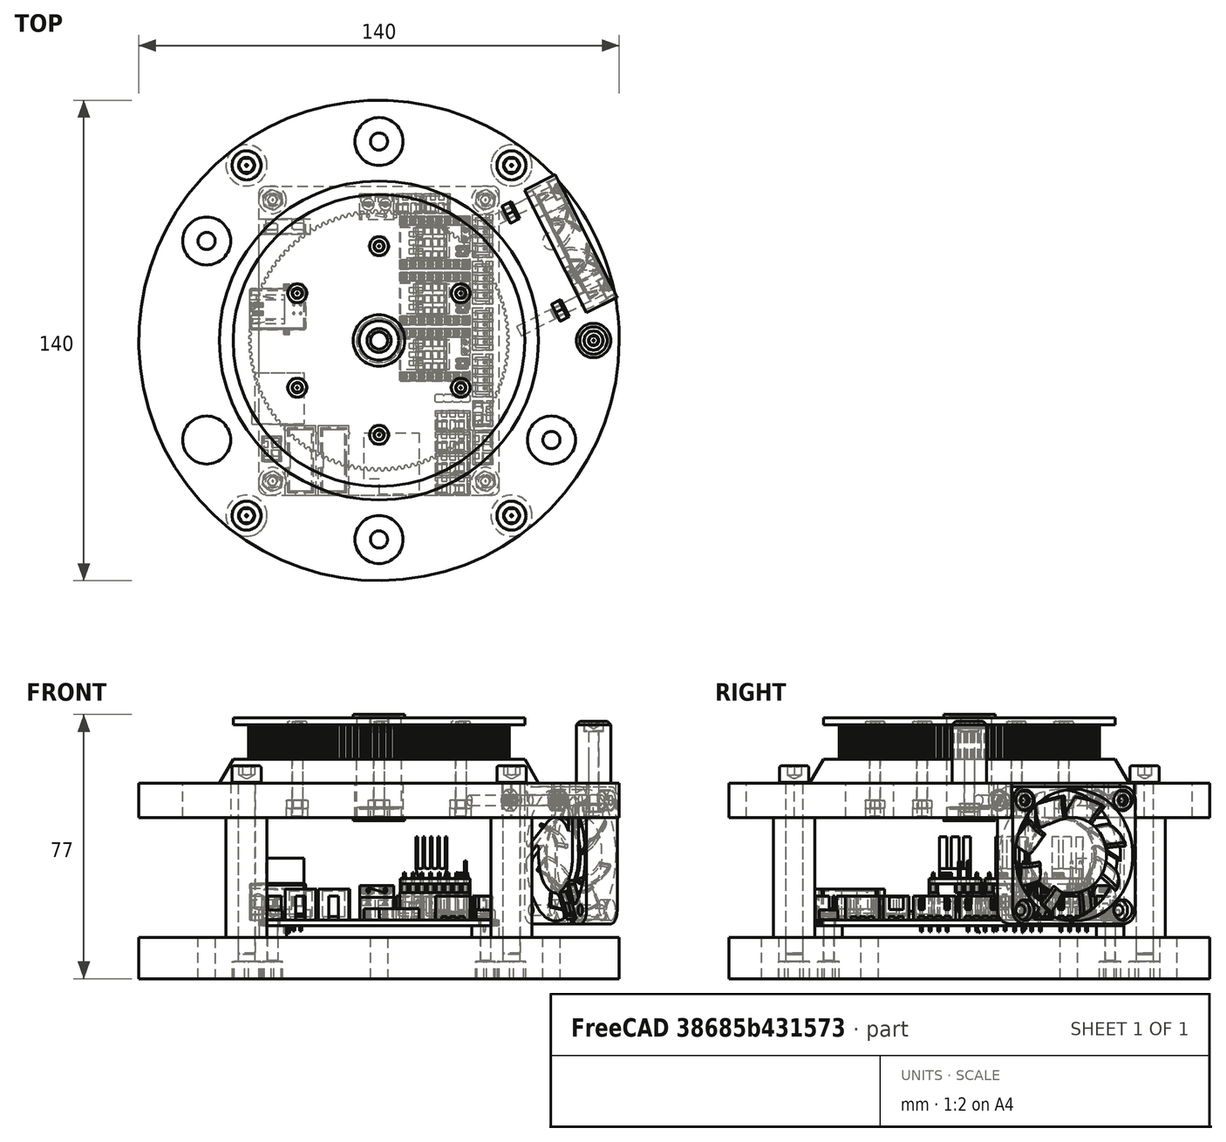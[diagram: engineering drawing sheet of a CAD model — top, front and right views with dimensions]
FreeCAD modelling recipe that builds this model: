
FCSTD DOCUMENT  (FreeCAD 0.20R29410 (Git))
Label: #0_ASSEMBLY_MAIN_BASE
License: All rights reserved
LicenseURL: http://en.wikipedia.org/wiki/All_rights_reserved
objects: Part::FeaturePython×38, App::FeaturePython×33
note: 38 computed .brp shape members not serialized (recipe doc carries the construction recipe); baked Part::Feature solids carry a one-line shape summary decoded from their .brp

FEATURE [Part::FeaturePython] b__1_BaseFloor_001_  label="#1_BaseFloor_001"  # a2plus imported part (geometry in sourceFile) (typed FeaturePython)
  a2p_Version = 0.4.60k
  fixedPosition = true
  objectType = a2pPart
  sourceFile = .\#1_BaseFloor.FCStd
  subassemblyImport = false
  timeLastImport = 1.68285e+09
  updateColors = true
FEATURE [Part::FeaturePython] b__2_BaseSpacers_001_  label="#2_BaseSpacers_001"  # a2plus imported part (geometry in sourceFile) (typed FeaturePython)
  Placement = pos=(38.6,-51.05,12) rot=(0,0,1;0rad)
  a2p_Version = 0.4.60k
  fixedPosition = false
  objectType = a2pPart
  sourceFile = .\#2_BaseSpacers.FCStd
  subassemblyImport = false
  timeLastImport = 1.68285e+09
  updateColors = true
FEATURE [Part::FeaturePython] b__3_BaseTop_001_  label="#3_BaseTop_001"  # a2plus imported part (geometry in sourceFile) (typed FeaturePython)
  Placement = pos=(-9e-15,-7.13554e-09,47) rot=(0,0,1;0rad)
  a2p_Version = 0.4.60k
  fixedPosition = false
  objectType = a2pPart
  sourceFile = .\#3_BaseTop.FCStd
  subassemblyImport = false
  timeLastImport = 1.68294e+09
  updateColors = true
FEATURE [Part::FeaturePython] b__2_BaseSpacers_001_001  label="#2_BaseSpacers_002"  # a2plus imported part (geometry in sourceFile) (typed FeaturePython)
  Placement = pos=(-38.6,-51.05,12) rot=(0,0,1;0rad)
  a2p_Version = 0.4.60k
  fixedPosition = false
  objectType = a2pPart
  sourceFile = .\#2_BaseSpacers.FCStd
  subassemblyImport = false
  timeLastImport = 1.68285e+09
  updateColors = true
FEATURE [Part::FeaturePython] b__2_BaseSpacers_001_002  label="#2_BaseSpacers_003"  # a2plus imported part (geometry in sourceFile) (typed FeaturePython)
  Placement = pos=(-38.6,51.05,12) rot=(0,0,1;0rad)
  a2p_Version = 0.4.60k
  fixedPosition = false
  objectType = a2pPart
  sourceFile = .\#2_BaseSpacers.FCStd
  subassemblyImport = false
  timeLastImport = 1.68285e+09
  updateColors = true
FEATURE [Part::FeaturePython] b__2_BaseSpacers_001_003  label="#2_BaseSpacers_004"  # a2plus imported part (geometry in sourceFile) (typed FeaturePython)
  Placement = pos=(38.6,51.05,12) rot=(0,0,1;0rad)
  a2p_Version = 0.4.60k
  fixedPosition = false
  objectType = a2pPart
  sourceFile = .\#2_BaseSpacers.FCStd
  subassemblyImport = false
  timeLastImport = 1.68285e+09
  updateColors = true
FEATURE [Part::FeaturePython] b_404010_Fan_v51_001_  label="4010Fan"  # a2plus imported part (geometry in sourceFile) (typed FeaturePython)
  Placement = pos=(51.4397,25.9841,36) rot=(0,0,-1;1.10305rad)
  a2p_Version = 0.4.60k
  fixedPosition = false
  objectType = a2pPart
  sourceFile = .\..\..\..\..\..\Downloads\404010 Fan v5.step
  subassemblyImport = false
  timeLastImport = 1.68849e+09
  updateColors = true
FEATURE [App::FeaturePython] circularEdge_001  label="circularEdge_001__#3_BaseTop_001"  # a2plus constraint (typed FeaturePython)
  Object1 = b_404010_Fan_v51_001_
  Object2 = b__3_BaseTop_001_
  ParentTreeObject = -> b_404010_Fan_v51_001_
  SubElement1 = Edge119
  SubElement2 = Edge96
  Suppressed = false
  Type = circularEdge
  directionConstraint = 1
  lockRotation = false
  offset = 0
FEATURE [App::FeaturePython] circularEdge_001_mirror  label="circularEdge_001__404010 Fan v51_001"  # a2plus constraint (typed FeaturePython)
  Object1 = b_404010_Fan_v51_001_
  Object2 = b__3_BaseTop_001_
  ParentTreeObject = -> b__3_BaseTop_001_
  SubElement1 = Edge119
  SubElement2 = Edge96
  Suppressed = false
  Type = circularEdge
  directionConstraint = 1
  lockRotation = false
  offset = 0
FEATURE [Part::FeaturePython] b__4_BasePulley120T_001_  label="#4_BasePulley120T_001"  # a2plus imported part (geometry in sourceFile) (typed FeaturePython)
  Placement = pos=(-38.1972,-38.1972,64) rot=(0,0,1;0rad)
  a2p_Version = 0.4.60k
  fixedPosition = false
  objectType = a2pPart
  sourceFile = .\#4_BasePulley120T.FCStd
  subassemblyImport = false
  timeLastImport = 1.68293e+09
  updateColors = true
FEATURE [App::FeaturePython] circularEdge_002  label="circularEdge_002__#3_BaseTop_001"  # a2plus constraint (typed FeaturePython)
  Object1 = b__4_BasePulley120T_001_
  Object2 = b__3_BaseTop_001_
  ParentTreeObject = -> b__4_BasePulley120T_001_
  SubElement1 = Edge2542
  SubElement2 = Edge151
  Suppressed = false
  Type = circularEdge
  directionConstraint = 0
  lockRotation = false
  offset = 0
FEATURE [App::FeaturePython] circularEdge_002_mirror  label="circularEdge_002__#4_BasePulley120T_001"  # a2plus constraint (typed FeaturePython)
  Object1 = b__4_BasePulley120T_001_
  Object2 = b__3_BaseTop_001_
  ParentTreeObject = -> b__3_BaseTop_001_
  SubElement1 = Edge2542
  SubElement2 = Edge151
  Suppressed = false
  Type = circularEdge
  directionConstraint = 0
  lockRotation = false
  offset = 0
FEATURE [App::FeaturePython] circularEdge_003  label="circularEdge_003__#3_BaseTop_001"  # a2plus constraint (typed FeaturePython)
  Object1 = b__4_BasePulley120T_001_
  Object2 = b__3_BaseTop_001_
  ParentTreeObject = -> b__4_BasePulley120T_001_
  SubElement1 = Edge2542
  SubElement2 = Edge151
  Suppressed = false
  Type = circularEdge
  directionConstraint = 0
  lockRotation = false
  offset = 0
FEATURE [App::FeaturePython] circularEdge_003_mirror  label="circularEdge_003__#4_BasePulley120T_001"  # a2plus constraint (typed FeaturePython)
  Object1 = b__4_BasePulley120T_001_
  Object2 = b__3_BaseTop_001_
  ParentTreeObject = -> b__3_BaseTop_001_
  SubElement1 = Edge2542
  SubElement2 = Edge151
  Suppressed = false
  Type = circularEdge
  directionConstraint = 0
  lockRotation = false
  offset = 0
FEATURE [App::FeaturePython] circularEdge_004  label="circularEdge_004__#1_BaseFloor_001"  # a2plus constraint (typed FeaturePython)
  Object1 = b__2_BaseSpacers_001_
  Object2 = b__1_BaseFloor_001_
  ParentTreeObject = -> b__2_BaseSpacers_001_
  SubElement1 = Edge2
  SubElement2 = Edge60
  Suppressed = false
  Type = circularEdge
  directionConstraint = 0
  lockRotation = false
  offset = 0
FEATURE [App::FeaturePython] circularEdge_004_mirror  label="circularEdge_004__#2_BaseSpacers_001"  # a2plus constraint (typed FeaturePython)
  Object1 = b__2_BaseSpacers_001_
  Object2 = b__1_BaseFloor_001_
  ParentTreeObject = -> b__1_BaseFloor_001_
  SubElement1 = Edge2
  SubElement2 = Edge60
  Suppressed = false
  Type = circularEdge
  directionConstraint = 0
  lockRotation = false
  offset = 0
FEATURE [App::FeaturePython] circularEdge_005  label="circularEdge_005__#2_BaseSpacers_001"  # a2plus constraint (typed FeaturePython)
  Object1 = b__3_BaseTop_001_
  Object2 = b__2_BaseSpacers_001_
  ParentTreeObject = -> b__3_BaseTop_001_
  SubElement1 = Edge24
  SubElement2 = Edge6
  Suppressed = false
  Type = circularEdge
  directionConstraint = 0
  lockRotation = false
  offset = 0
FEATURE [App::FeaturePython] circularEdge_005_mirror  label="circularEdge_005__#3_BaseTop_001"  # a2plus constraint (typed FeaturePython)
  Object1 = b__3_BaseTop_001_
  Object2 = b__2_BaseSpacers_001_
  ParentTreeObject = -> b__2_BaseSpacers_001_
  SubElement1 = Edge24
  SubElement2 = Edge6
  Suppressed = false
  Type = circularEdge
  directionConstraint = 0
  lockRotation = false
  offset = 0
FEATURE [App::FeaturePython] axisCoincident_001  label="axisCoincident_001__#1_BaseFloor_001"  # a2plus constraint (typed FeaturePython)
  Object1 = b__2_BaseSpacers_001_003
  Object2 = b__1_BaseFloor_001_
  ParentTreeObject = -> b__2_BaseSpacers_001_003
  SubElement1 = Edge2
  SubElement2 = Edge69
  Suppressed = false
  Type = axial
  directionConstraint = 0
  lockRotation = false
FEATURE [App::FeaturePython] axisCoincident_001_mirror  label="axisCoincident_001__#2_BaseSpacers_004"  # a2plus constraint (typed FeaturePython)
  Object1 = b__2_BaseSpacers_001_003
  Object2 = b__1_BaseFloor_001_
  ParentTreeObject = -> b__1_BaseFloor_001_
  SubElement1 = Edge2
  SubElement2 = Edge69
  Suppressed = false
  Type = axial
  directionConstraint = 0
  lockRotation = false
FEATURE [App::FeaturePython] circularEdge_006  label="circularEdge_006__#1_BaseFloor_001"  # a2plus constraint (typed FeaturePython)
  Object1 = b__2_BaseSpacers_001_003
  Object2 = b__1_BaseFloor_001_
  ParentTreeObject = -> b__2_BaseSpacers_001_003
  SubElement1 = Edge2
  SubElement2 = Edge69
  Suppressed = false
  Type = circularEdge
  directionConstraint = 0
  lockRotation = false
  offset = 0
FEATURE [App::FeaturePython] circularEdge_006_mirror  label="circularEdge_006__#2_BaseSpacers_004"  # a2plus constraint (typed FeaturePython)
  Object1 = b__2_BaseSpacers_001_003
  Object2 = b__1_BaseFloor_001_
  ParentTreeObject = -> b__1_BaseFloor_001_
  SubElement1 = Edge2
  SubElement2 = Edge69
  Suppressed = false
  Type = circularEdge
  directionConstraint = 0
  lockRotation = false
  offset = 0
FEATURE [App::FeaturePython] circularEdge_007  label="circularEdge_007__#1_BaseFloor_001"  # a2plus constraint (typed FeaturePython)
  Object1 = b__2_BaseSpacers_001_002
  Object2 = b__1_BaseFloor_001_
  ParentTreeObject = -> b__2_BaseSpacers_001_002
  SubElement1 = Edge2
  SubElement2 = Edge65
  Suppressed = false
  Type = circularEdge
  directionConstraint = 0
  lockRotation = false
  offset = 0
FEATURE [App::FeaturePython] circularEdge_007_mirror  label="circularEdge_007__#2_BaseSpacers_003"  # a2plus constraint (typed FeaturePython)
  Object1 = b__2_BaseSpacers_001_002
  Object2 = b__1_BaseFloor_001_
  ParentTreeObject = -> b__1_BaseFloor_001_
  SubElement1 = Edge2
  SubElement2 = Edge65
  Suppressed = false
  Type = circularEdge
  directionConstraint = 0
  lockRotation = false
  offset = 0
FEATURE [App::FeaturePython] circularEdge_008  label="circularEdge_008__#1_BaseFloor_001"  # a2plus constraint (typed FeaturePython)
  Object1 = b__2_BaseSpacers_001_001
  Object2 = b__1_BaseFloor_001_
  ParentTreeObject = -> b__2_BaseSpacers_001_001
  SubElement1 = Edge2
  SubElement2 = Edge57
  Suppressed = false
  Type = circularEdge
  directionConstraint = 0
  lockRotation = false
  offset = 0
FEATURE [App::FeaturePython] circularEdge_008_mirror  label="circularEdge_008__#2_BaseSpacers_002"  # a2plus constraint (typed FeaturePython)
  Object1 = b__2_BaseSpacers_001_001
  Object2 = b__1_BaseFloor_001_
  ParentTreeObject = -> b__1_BaseFloor_001_
  SubElement1 = Edge2
  SubElement2 = Edge57
  Suppressed = false
  Type = circularEdge
  directionConstraint = 0
  lockRotation = false
  offset = 0
FEATURE [Part::FeaturePython] Screw  label="M3x25-Tornillo"  # Fasteners workbench fastener (typed FeaturePython)
  Placement = pos=(-23.8157,-13.75,72) rot=(0,0,1;0rad)
  baseObject = -> b__4_BasePulley120T_001_ [Edge2555]
  diameter = 4
  invert = false
  leftHanded = false
  length = 10
  lengthCustom = 25
  matchOuter = false
  offset = 0
  thread = false
  type = 45
FEATURE [Part::FeaturePython] Screw001  label="M3x25-Tornillo018"  # Fasteners workbench fastener (typed FeaturePython)
  Placement = pos=(-23.8157,13.75,72) rot=(0,0,1;0rad)
  baseObject = -> b__4_BasePulley120T_001_ [Edge2556]
  diameter = 4
  invert = false
  leftHanded = false
  length = 10
  lengthCustom = 25
  matchOuter = false
  offset = 0
  thread = false
  type = 45
FEATURE [Part::FeaturePython] Screw002  label="M3x25-Tornillo019"  # Fasteners workbench fastener (typed FeaturePython)
  Placement = pos=(7.1e-15,27.5,72) rot=(0,0,1;0rad)
  baseObject = -> b__4_BasePulley120T_001_ [Edge2553]
  diameter = 4
  invert = false
  leftHanded = false
  length = 10
  lengthCustom = 25
  matchOuter = false
  offset = 0
  thread = false
  type = 45
FEATURE [Part::FeaturePython] Screw003  label="M3x25-Tornillo020"  # Fasteners workbench fastener (typed FeaturePython)
  Placement = pos=(23.8157,13.75,72) rot=(0,0,1;0rad)
  baseObject = -> b__4_BasePulley120T_001_ [Edge2552]
  diameter = 4
  invert = false
  leftHanded = false
  length = 10
  lengthCustom = 25
  matchOuter = false
  offset = 0
  thread = false
  type = 45
FEATURE [Part::FeaturePython] Screw004  label="M3x25-Tornillo021"  # Fasteners workbench fastener (typed FeaturePython)
  Placement = pos=(23.8157,-13.75,72) rot=(0,0,1;0rad)
  baseObject = -> b__4_BasePulley120T_001_ [Edge2551]
  diameter = 4
  invert = false
  leftHanded = false
  length = 10
  lengthCustom = 25
  matchOuter = false
  offset = 0
  thread = false
  type = 45
FEATURE [Part::FeaturePython] Screw005  label="M3x25-Tornillo022"  # Fasteners workbench fastener (typed FeaturePython)
  Placement = pos=(-7.1e-15,-27.5,72) rot=(0,0,1;0rad)
  baseObject = -> b__4_BasePulley120T_001_ [Edge2554]
  diameter = 4
  invert = false
  leftHanded = false
  length = 10
  lengthCustom = 25
  matchOuter = false
  offset = 0
  thread = false
  type = 45
FEATURE [Part::FeaturePython] Screw006  label="M5x50-Tornillo"  # Fasteners workbench fastener (typed FeaturePython)
  Placement = pos=(38.6,51.05,57) rot=(0,0,1;0rad)
  baseObject = -> b__3_BaseTop_001_ [Edge92]
  diameter = 6
  invert = false
  leftHanded = false
  length = 12
  lengthCustom = 50
  matchOuter = false
  offset = 0
  thread = false
  type = 45
FEATURE [Part::FeaturePython] Screw007  label="M5x50-Tornillo007"  # Fasteners workbench fastener (typed FeaturePython)
  Placement = pos=(38.6,-51.05,57) rot=(0,0,1;0rad)
  baseObject = -> b__3_BaseTop_001_ [Edge77]
  diameter = 6
  invert = false
  leftHanded = false
  length = 12
  lengthCustom = 50
  matchOuter = false
  offset = 0
  thread = false
  type = 45
FEATURE [Part::FeaturePython] Screw008  label="M5x50-Tornillo008"  # Fasteners workbench fastener (typed FeaturePython)
  Placement = pos=(-38.6,-51.05,57) rot=(0,0,1;0rad)
  baseObject = -> b__3_BaseTop_001_ [Edge74]
  diameter = 6
  invert = false
  leftHanded = false
  length = 12
  lengthCustom = 50
  matchOuter = false
  offset = 0
  thread = false
  type = 45
FEATURE [Part::FeaturePython] Screw009  label="M5x50-Tornillo009"  # Fasteners workbench fastener (typed FeaturePython)
  Placement = pos=(-38.6,51.05,57) rot=(0,0,1;0rad)
  baseObject = -> b__3_BaseTop_001_ [Edge81]
  diameter = 6
  invert = false
  leftHanded = false
  length = 12
  lengthCustom = 50
  matchOuter = false
  offset = 0
  thread = false
  type = 45
FEATURE [Part::FeaturePython] Screw010  label="M3x16-Tornillo"  # Fasteners workbench fastener (typed FeaturePython)
  Placement = pos=(64.9019,14.8588,52) rot=(-0.450878,0.892586,0;1.5708rad)
  baseObject = -> b_404010_Fan_v51_001_ [Edge73]
  diameter = 4
  invert = false
  leftHanded = false
  length = 10
  lengthCustom = 16
  matchOuter = false
  offset = 0
  thread = false
  type = 45
FEATURE [Part::FeaturePython] Screw011  label="M3x16-Tornillo001"  # Fasteners workbench fastener (typed FeaturePython)
  Placement = pos=(50.4738,43.4216,52) rot=(-0.450878,0.892586,0;1.5708rad)
  baseObject = -> b_404010_Fan_v51_001_ [Edge61]
  diameter = 4
  invert = false
  leftHanded = false
  length = 10
  lengthCustom = 16
  matchOuter = false
  offset = 0
  thread = false
  type = 45
FEATURE [Part::FeaturePython] b__6_BaseRotationLimit_001_  label="#6_BaseRotationLimit_001"  # a2plus imported part (geometry in sourceFile) (typed FeaturePython)
  Placement = pos=(62.5,-7.13554e-09,57.0012) rot=(0,0,1;0rad)
  a2p_Version = 0.4.60k
  fixedPosition = false
  objectType = a2pPart
  sourceFile = .\#6_BaseRotationLimit.FCStd
  subassemblyImport = false
  timeLastImport = 1.68294e+09
  updateColors = true
FEATURE [App::FeaturePython] circularEdge_009  label="circularEdge_009__#3_BaseTop_001"  # a2plus constraint (typed FeaturePython)
  Object1 = b__6_BaseRotationLimit_001_
  Object2 = b__3_BaseTop_001_
  ParentTreeObject = -> b__6_BaseRotationLimit_001_
  SubElement1 = Edge3
  SubElement2 = Edge83
  Suppressed = false
  Type = circularEdge
  directionConstraint = 0
  lockRotation = false
  offset = 0
FEATURE [App::FeaturePython] circularEdge_009_mirror  label="circularEdge_009__#6_BaseRotationLimit_001"  # a2plus constraint (typed FeaturePython)
  Object1 = b__6_BaseRotationLimit_001_
  Object2 = b__3_BaseTop_001_
  ParentTreeObject = -> b__3_BaseTop_001_
  SubElement1 = Edge3
  SubElement2 = Edge83
  Suppressed = false
  Type = circularEdge
  directionConstraint = 0
  lockRotation = false
  offset = 0
FEATURE [Part::FeaturePython] Screw012  label="M3x25-Tornillo023"  # Fasteners workbench fastener (typed FeaturePython)
  Placement = pos=(62.5,-7.13554e-09,72.0012) rot=(0,0,1;0rad)
  baseObject = -> b__6_BaseRotationLimit_001_ [Edge9]
  diameter = 4
  invert = true
  leftHanded = false
  length = 8
  lengthCustom = 25
  matchOuter = false
  offset = 0
  thread = false
  type = 45
FEATURE [Part::FeaturePython] b_Mks1_001_  label="Mks1_001"  # a2plus imported part (geometry in sourceFile) (typed FeaturePython)
  Placement = pos=(-28.4749,-43.7494,28.3991) rot=(0.57735,0.57735,0.57735;2.0944rad)
  a2p_Version = 0.4.60k
  fixedPosition = false
  objectType = a2pPart
  sourceFile = .\..\..\..\..\..\Downloads\Mks.STEP
  subassemblyImport = false
  timeLastImport = 1.68849e+09
  updateColors = true
FEATURE [App::FeaturePython] circularEdge_010  label="circularEdge_010__#1_BaseFloor_001"  # a2plus constraint (typed FeaturePython)
  Object1 = b_Mks1_001_
  Object2 = b__1_BaseFloor_001_
  ParentTreeObject = -> b_Mks1_001_
  SubElement1 = Edge10771
  SubElement2 = Edge193
  Suppressed = false
  Type = circularEdge
  directionConstraint = 0
  lockRotation = false
  offset = 0
FEATURE [App::FeaturePython] circularEdge_010_mirror  label="circularEdge_010__Mks1_001"  # a2plus constraint (typed FeaturePython)
  Object1 = b_Mks1_001_
  Object2 = b__1_BaseFloor_001_
  ParentTreeObject = -> b__1_BaseFloor_001_
  SubElement1 = Edge10771
  SubElement2 = Edge193
  Suppressed = false
  Type = circularEdge
  directionConstraint = 0
  lockRotation = false
  offset = 0
FEATURE [App::FeaturePython] circularEdge_011  label="circularEdge_011__#1_BaseFloor_001"  # a2plus constraint (typed FeaturePython)
  Object1 = b_Mks1_001_
  Object2 = b__1_BaseFloor_001_
  ParentTreeObject = -> b_Mks1_001_
  SubElement1 = Edge10775
  SubElement2 = Edge194
  Suppressed = false
  Type = circularEdge
  directionConstraint = 0
  lockRotation = false
  offset = 0
FEATURE [App::FeaturePython] circularEdge_011_mirror  label="circularEdge_011__Mks1_001"  # a2plus constraint (typed FeaturePython)
  Object1 = b_Mks1_001_
  Object2 = b__1_BaseFloor_001_
  ParentTreeObject = -> b__1_BaseFloor_001_
  SubElement1 = Edge10775
  SubElement2 = Edge194
  Suppressed = false
  Type = circularEdge
  directionConstraint = 0
  lockRotation = false
  offset = 0
FEATURE [Part::FeaturePython] b_F6951_001_  label="F6951_001"  # a2plus imported part (geometry in sourceFile) (typed FeaturePython)
  Placement = pos=(9.797e-12,-7.14046e-09,73) rot=(0,0,1;0rad)
  a2p_Version = 0.4.60k
  fixedPosition = false
  objectType = a2pPart
  sourceFile = .\..\Complements\F695.step
  subassemblyImport = false
  timeLastImport = 1.6885e+09
  updateColors = true
FEATURE [Part::FeaturePython] b_F6951_001_001  label="F6951_002"  # a2plus imported part (geometry in sourceFile) (typed FeaturePython)
  Placement = pos=(-1.73663e-08,-3.91819e-08,50) rot=(0.879228,-0.476402,0;3.14159rad)
  a2p_Version = 0.4.60k
  fixedPosition = false
  objectType = a2pPart
  sourceFile = .\..\Complements\F695.step
  subassemblyImport = false
  timeLastImport = 1.6885e+09
  updateColors = true
FEATURE [App::FeaturePython] circularEdge_012  label="circularEdge_012__#4_BasePulley120T_001"  # a2plus constraint (typed FeaturePython)
  Object1 = b_F6951_001_
  Object2 = b__4_BasePulley120T_001_
  ParentTreeObject = -> b_F6951_001_
  SubElement1 = Edge18
  SubElement2 = Edge849
  Suppressed = false
  Type = circularEdge
  directionConstraint = 0
  lockRotation = false
  offset = 0
FEATURE [App::FeaturePython] circularEdge_012_mirror  label="circularEdge_012__F6951_001"  # a2plus constraint (typed FeaturePython)
  Object1 = b_F6951_001_
  Object2 = b__4_BasePulley120T_001_
  ParentTreeObject = -> b__4_BasePulley120T_001_
  SubElement1 = Edge18
  SubElement2 = Edge849
  Suppressed = false
  Type = circularEdge
  directionConstraint = 0
  lockRotation = false
  offset = 0
FEATURE [App::FeaturePython] circularEdge_013  label="circularEdge_013__#3_BaseTop_001"  # a2plus constraint (typed FeaturePython)
  Object1 = b_F6951_001_001
  Object2 = b__3_BaseTop_001_
  ParentTreeObject = -> b_F6951_001_001
  SubElement1 = Edge18
  SubElement2 = Edge39
  Suppressed = false
  Type = circularEdge
  directionConstraint = 1
  lockRotation = false
  offset = 0
FEATURE [App::FeaturePython] circularEdge_013_mirror  label="circularEdge_013__F6951_002"  # a2plus constraint (typed FeaturePython)
  Object1 = b_F6951_001_001
  Object2 = b__3_BaseTop_001_
  ParentTreeObject = -> b__3_BaseTop_001_
  SubElement1 = Edge18
  SubElement2 = Edge39
  Suppressed = false
  Type = circularEdge
  directionConstraint = 1
  lockRotation = false
  offset = 0
FEATURE [Part::FeaturePython] Screw013  label="M3x12-Tornillo"  # Fasteners workbench fastener (typed FeaturePython)
  Placement = pos=(31,-41,17) rot=(0,0,1;0rad)
  baseObject = -> b__1_BaseFloor_001_ [Edge192]
  diameter = 4
  invert = false
  leftHanded = false
  length = 10
  lengthCustom = 12
  matchOuter = false
  offset = 1.5
  thread = false
  type = 45
FEATURE [Part::FeaturePython] Screw014  label="M3x12-Tornillo013"  # Fasteners workbench fastener (typed FeaturePython)
  Placement = pos=(-31,-41,17) rot=(0,0,1;0rad)
  baseObject = -> b__1_BaseFloor_001_ [Edge191]
  diameter = 4
  invert = false
  leftHanded = false
  length = 10
  lengthCustom = 12
  matchOuter = false
  offset = 1.5
  thread = false
  type = 45
FEATURE [Part::FeaturePython] Screw015  label="M3x12-Tornillo014"  # Fasteners workbench fastener (typed FeaturePython)
  Placement = pos=(-31,41,17) rot=(0,0,1;0rad)
  baseObject = -> b__1_BaseFloor_001_ [Edge193]
  diameter = 4
  invert = false
  leftHanded = false
  length = 10
  lengthCustom = 12
  matchOuter = false
  offset = 1.5
  thread = false
  type = 45
FEATURE [Part::FeaturePython] Screw016  label="M3x12-Tornillo015"  # Fasteners workbench fastener (typed FeaturePython)
  Placement = pos=(31,41,17) rot=(0,0,1;0rad)
  baseObject = -> b__1_BaseFloor_001_ [Edge194]
  diameter = 4
  invert = false
  leftHanded = false
  length = 10
  lengthCustom = 12
  matchOuter = false
  offset = 1.5
  thread = false
  type = 45
FEATURE [Part::FeaturePython] Nut  label="M3-Tuerca"  # Fasteners workbench fastener (typed FeaturePython)
  Placement = pos=(-9e-15,-27.5,52) rot=(1,0,0;3.14159rad)
  baseObject = -> b__3_BaseTop_001_ [Edge210]
  diameter = 4
  invert = true
  leftHanded = false
  matchOuter = false
  offset = 0
  thread = false
  type = 22
FEATURE [Part::FeaturePython] Nut001  label="M3-Tuerca001"  # Fasteners workbench fastener (typed FeaturePython)
  Placement = pos=(23.8157,-13.75,52) rot=(1,0,0;3.14159rad)
  baseObject = -> b__3_BaseTop_001_ [Edge212]
  diameter = 4
  invert = true
  leftHanded = false
  matchOuter = false
  offset = 0
  thread = false
  type = 22
FEATURE [Part::FeaturePython] Nut002  label="M3-Tuerca002"  # Fasteners workbench fastener (typed FeaturePython)
  Placement = pos=(23.8157,13.75,52) rot=(1,0,0;3.14159rad)
  baseObject = -> b__3_BaseTop_001_ [Edge221]
  diameter = 4
  invert = true
  leftHanded = false
  matchOuter = false
  offset = 0
  thread = false
  type = 22
FEATURE [Part::FeaturePython] Nut003  label="M3-Tuerca003"  # Fasteners workbench fastener (typed FeaturePython)
  Placement = pos=(-23.8157,-13.75,52) rot=(1,0,0;3.14159rad)
  baseObject = -> b__3_BaseTop_001_ [Edge211]
  diameter = 4
  invert = true
  leftHanded = false
  matchOuter = false
  offset = 0
  thread = false
  type = 22
FEATURE [Part::FeaturePython] Nut004  label="M3-Tuerca004"  # Fasteners workbench fastener (typed FeaturePython)
  Placement = pos=(-23.8157,13.75,52) rot=(1,0,0;3.14159rad)
  baseObject = -> b__3_BaseTop_001_ [Edge213]
  diameter = 4
  invert = true
  leftHanded = false
  matchOuter = false
  offset = 0
  thread = false
  type = 22
FEATURE [Part::FeaturePython] Nut005  label="M3-Tuerca005"  # Fasteners workbench fastener (typed FeaturePython)
  Placement = pos=(-5e-15,27.5,52) rot=(1,0,0;3.14159rad)
  baseObject = -> b__3_BaseTop_001_ [Edge220]
  diameter = 4
  invert = true
  leftHanded = false
  matchOuter = false
  offset = 0
  thread = false
  type = 22
FEATURE [Part::FeaturePython] Nut006  label="M3-Tuerca006"  # Fasteners workbench fastener (typed FeaturePython)
  Placement = pos=(62.5,-7.13554e-09,51) rot=(1,0,0;3.14159rad)
  baseObject = -> b__3_BaseTop_001_ [Edge207]
  diameter = 4
  invert = true
  leftHanded = false
  matchOuter = false
  offset = 0
  thread = false
  type = 22
FEATURE [Part::FeaturePython] Nut007  label="M3-Tuerca015"  # Fasteners workbench fastener (typed FeaturePython)
  Placement = pos=(53.6553,9.17784,52.0028) rot=(0.218242,-0.947785,0.232538;1.628rad)
  diameter = 4
  invert = false
  leftHanded = false
  matchOuter = false
  offset = 0
  thread = false
  type = 22
FEATURE [App::FeaturePython] circularEdge_014  label="circularEdge_014__#3_BaseTop_001"  # a2plus constraint (typed FeaturePython)
  Object1 = Nut007
  Object2 = b__3_BaseTop_001_
  ParentTreeObject = -> Nut007
  SubElement1 = Edge2
  SubElement2 = Edge193
  Suppressed = false
  Type = circularEdge
  directionConstraint = 1
  lockRotation = false
  offset = 0
FEATURE [App::FeaturePython] circularEdge_014_mirror  label="circularEdge_014__M3-Tuerca007"  # a2plus constraint (typed FeaturePython)
  Object1 = Nut007
  Object2 = b__3_BaseTop_001_
  ParentTreeObject = -> b__3_BaseTop_001_
  SubElement1 = Edge2
  SubElement2 = Edge193
  Suppressed = false
  Type = circularEdge
  directionConstraint = 1
  lockRotation = false
  offset = 0
FEATURE [App::FeaturePython] circularEdge_016_mirror001  label="circularEdge_016__M3-Tuerca010"  # a2plus constraint (typed FeaturePython)
  Object1 = Nut008
  Object2 = b__3_BaseTop_001_
  ParentTreeObject = -> b__3_BaseTop_001_
  SubElement1 = Edge2
  SubElement2 = Edge199
  Suppressed = false
  Type = circularEdge
  directionConstraint = 1
  lockRotation = false
  offset = 0
FEATURE [Part::FeaturePython] Nut008  label="M3-Tuerca016"  # Fasteners workbench fastener (typed FeaturePython)
  Placement = pos=(39.2272,37.7405,52.0028) rot=(0.226933,-0.947632,0.224712;1.62401rad)
  diameter = 4
  invert = false
  leftHanded = false
  matchOuter = false
  offset = 0
  thread = false
  type = 22
FEATURE [App::FeaturePython] circularEdge_015  label="circularEdge_015__#3_BaseTop_001"  # a2plus constraint (typed FeaturePython)
  Object1 = Nut008
  Object2 = b__3_BaseTop_001_
  ParentTreeObject = -> Nut008
  SubElement1 = Edge2
  SubElement2 = Edge199
  Suppressed = false
  Type = circularEdge
  directionConstraint = 1
  lockRotation = false
  offset = 0
FEATURE [App::FeaturePython] circularEdge_015_mirror  label="circularEdge_015__M3-Tuerca008"  # a2plus constraint (typed FeaturePython)
  Object1 = Nut008
  Object2 = b__3_BaseTop_001_
  ParentTreeObject = -> b__3_BaseTop_001_
  SubElement1 = Edge2
  SubElement2 = Edge199
  Suppressed = false
  Type = circularEdge
  directionConstraint = 1
  lockRotation = false
  offset = 0
